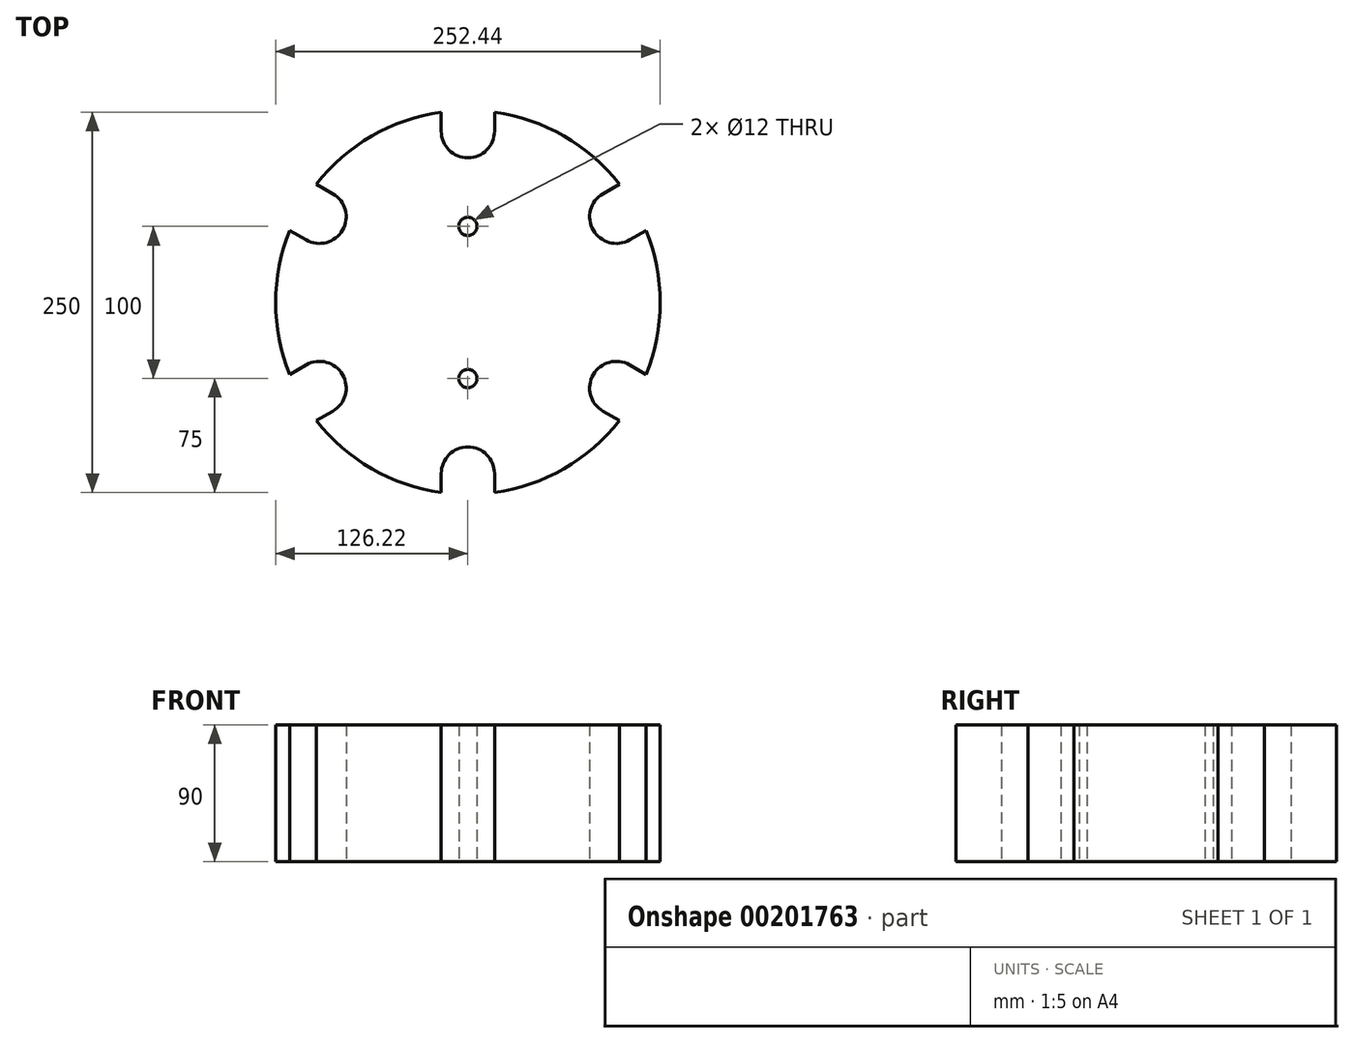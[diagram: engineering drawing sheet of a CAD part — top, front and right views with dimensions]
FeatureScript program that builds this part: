
annotation { "Feature Type Name" : "Feature", "Feature Type Description" : "" }
export const myFeature = defineFeature(function(context is Context, id is Id, definition is map)
    precondition{}
    {
        {
            var Q0;
            Q0=qCreatedBy(makeId("Top.planeOp"),FACE);
            var sketch = newSketch(context, id + "F0", { "sketchPlane" : qUnion([Q0])});
            skCircle(sketch, "E0", {"center": v(0, 0) * mm, "radius": 112.5 * mm, "construction": true});
            skCircle(sketch, "E1", {"center": v(0, 50) * mm, "radius": 6 * mm});
            skCircle(sketch, "E2", {"center": v(0, -50) * mm, "radius": 6 * mm});
            skLineSegment(sketch, "E3.0", {"start": v(17.5, 112.5) * mm, "end": v(17.5, 125) * mm});
            skArc(sketch, "E3.1", {"start": v(17.5, 112.5) * mm, "mid": v(0, 95) * mm, "end": v(-17.5, 112.5) * mm});
            skLineSegment(sketch, "E3.2", {"start": v(-17.5, 112.5) * mm, "end": v(-17.5, 125) * mm});
            skArc(sketch, "E4", {"start": v(-17.5, 125) * mm, "mid": v(-63.1, 109.3) * mm, "end": v(-99.5, 77.66) * mm});
            skLineSegment(sketch, "E5.1.0", {"start": v(-106.18, 41.1) * mm, "end": v(-117, 47.34) * mm});
            skArc(sketch, "E5.1.1", {"start": v(-88.68, 71.4) * mm, "mid": v(-82.27, 47.5) * mm, "end": v(-106.18, 41.1) * mm});
            skLineSegment(sketch, "E5.1.2", {"start": v(-88.68, 71.4) * mm, "end": v(-99.5, 77.66) * mm});
            skLineSegment(sketch, "E5.2.0", {"start": v(-88.68, -71.4) * mm, "end": v(-99.5, -77.66) * mm});
            skArc(sketch, "E5.2.1", {"start": v(-106.18, -41.1) * mm, "mid": v(-82.27, -47.5) * mm, "end": v(-88.68, -71.4) * mm});
            skLineSegment(sketch, "E5.2.2", {"start": v(-106.18, -41.1) * mm, "end": v(-117, -47.34) * mm});
            skLineSegment(sketch, "E5.3.0", {"start": v(17.5, -112.5) * mm, "end": v(17.5, -125) * mm});
            skArc(sketch, "E5.3.1", {"start": v(-17.5, -112.5) * mm, "mid": v(0, -95) * mm, "end": v(17.5, -112.5) * mm});
            skLineSegment(sketch, "E5.3.2", {"start": v(-17.5, -112.5) * mm, "end": v(-17.5, -125) * mm});
            skLineSegment(sketch, "E5.4.0", {"start": v(106.18, -41.1) * mm, "end": v(117, -47.34) * mm});
            skArc(sketch, "E5.4.1", {"start": v(88.68, -71.4) * mm, "mid": v(82.27, -47.5) * mm, "end": v(106.18, -41.1) * mm});
            skLineSegment(sketch, "E5.4.2", {"start": v(88.68, -71.4) * mm, "end": v(99.5, -77.66) * mm});
            skLineSegment(sketch, "E5.5.0", {"start": v(88.68, 71.4) * mm, "end": v(99.5, 77.66) * mm});
            skArc(sketch, "E5.5.1", {"start": v(106.18, 41.1) * mm, "mid": v(82.27, 47.5) * mm, "end": v(88.68, 71.4) * mm});
            skLineSegment(sketch, "E5.5.2", {"start": v(106.18, 41.1) * mm, "end": v(117, 47.34) * mm});
            skArc(sketch, "E6.trimOffspring", {"start": v(99.5, 77.66) * mm, "mid": v(63.1, 109.3) * mm, "end": v(17.5, 125) * mm});
            skArc(sketch, "E7.trimOffspring", {"start": v(117, -47.34) * mm, "mid": v(126.22, 0) * mm, "end": v(117, 47.34) * mm});
            skArc(sketch, "E8.trimOffspring", {"start": v(17.5, -125) * mm, "mid": v(63.1, -109.3) * mm, "end": v(99.5, -77.66) * mm});
            skArc(sketch, "E9.trimOffspring", {"start": v(-99.5, -77.66) * mm, "mid": v(-63.1, -109.3) * mm, "end": v(-17.5, -125) * mm});
            skArc(sketch, "E10.trimOffspring", {"start": v(-117, 47.34) * mm, "mid": v(-126.22, 0) * mm, "end": v(-117, -47.34) * mm});
            skCircle(sketch, "E11", {"center": v(0, 0) * mm, "radius": 126.22 * mm, "construction": true});
            skSolve(sketch);
        }
        {
            var Q0;
            Q0=makeQuery(id+"F0.imprint","IMPRINT",FACE,{"disambiguationData":[TD([[makeQuery(id+"F0.imprint","IMPRINT",EDGE,{"derivedFrom":sQuery(id+"F0.wireOp",EDGE,"E1")}),-1.0]])]});
            extrude(context, id + "F1", {"entities" : qUnion([Q0]), "depth" : 90 * mm});
        }
    });
